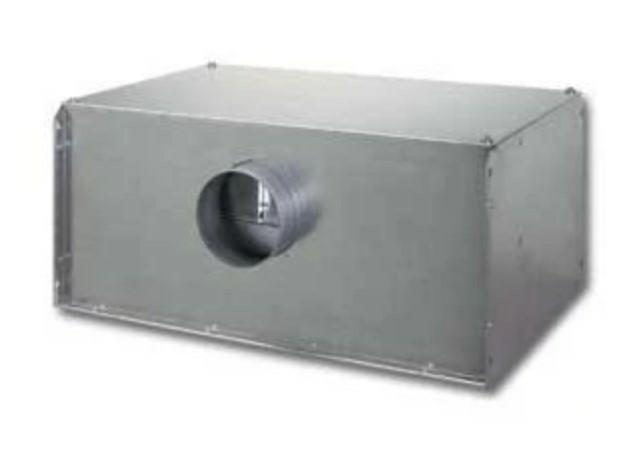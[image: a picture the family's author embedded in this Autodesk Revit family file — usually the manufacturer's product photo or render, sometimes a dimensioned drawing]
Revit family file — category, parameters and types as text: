
# Revit family: CADS_Vent-Axia_MechEquip_Fan_QPTW_QuietPackTwin - SUPPLY
name_source: partatom
category: Mechanical Equipment
units: mm (PartAtom-declared; Revit-internal decimal feet)

## family parameters
Classification = None
Cut with Voids When Loaded = No
Host = Face
OmniClass Number = 23.75.35.17.11
OmniClass Title = Fans for Air Ductwork
Part Type = Normal
Room Calculation Point = No
Round Connector Dimension = Use Diameter
Shared = No

## types (7) — shared parameters
Air Flow = 0.0 L/s
AirflowRateRange = 0.0 L/s
AssemblyPlace = UNKNOWN
AssetType = FIXED
Default Elevation = 1219 mm
DurationUnit = Year
EBHoffset = 206 mm
EBVoffset = 80 mm
ExteriorInsulation = No
Fitting Type = Ignore
GrossWeight = 0.00 kg
HasProtectiveEarth = No
IsExtendedWarranty = No
ManufacturerAddress = Fleming Way
Crawley 
RH10 9YX
Quantity = 1
RatedCurrent = 0 A
RatedVoltage = 0 V
Status = New
WarrantyGuarantor = Vent-Axia Limited
WorkingPressure = 0.0 Pa
zero-valued in all types: CADS_Index, CADS_Usage, ExpectedServiceLife, H, NumberOfPoles, OutOffset, W

## per-type parameters (varying)
| type | L | ModelReference | NominalDiameter | NominalHeight | NominalLength | NominalWidth | SpigotCLHeight | Type Image |
| QPTW100C | 590 mm  [stored 1.9357 ft] | QPTW100C QUIET PACK TWIN FAN | 100 mm  [stored 0.328084 ft] | 256 mm  [stored 0.839895 ft] | 610 mm  [stored 2.00131 ft] | 622 mm  [stored 2.04068 ft] | 128 mm  [stored 0.419948 ft] | <None> |
| QPTW125C | 590 mm  [stored 1.9357 ft] | QPTW125C QUIET PACK TWIN FAN | 125 mm  [stored 0.410105 ft] | 256 mm  [stored 0.839895 ft] | 610 mm  [stored 2.00131 ft] | 622 mm  [stored 2.04068 ft] | 128 mm  [stored 0.419948 ft] | <None> |
| QPTW150C | 590 mm  [stored 1.9357 ft] | QPTW150C QUIET PACK TWIN FAN | 150 mm | 256 mm  [stored 0.839895 ft] | 610 mm  [stored 2.00131 ft] | 622 mm  [stored 2.04068 ft] | 128 mm  [stored 0.419948 ft] | <None> |
| QPTW160C | 590 mm  [stored 1.9357 ft] | QPTW160C QUIET PACK TWIN FAN | 160 mm  [stored 0.524934 ft] | 256 mm  [stored 0.839895 ft] | 610 mm  [stored 2.00131 ft] | 622 mm  [stored 2.04068 ft] | 128 mm  [stored 0.419948 ft] | <None> |
| QPTW250C | 905 mm  [stored 2.96916 ft] | QPTW250C QUIET PACK TWIN FAN | 250 mm  [stored 0.82021 ft] | 354 mm  [stored 1.16142 ft] | 925 mm  [stored 3.03478 ft] | 829 mm  [stored 2.71982 ft] | 177 mm  [stored 0.580709 ft] | <None> |
| QPTW315C | 1235 mm  [stored 4.05184 ft] | QPTW315C QUIET PACK TWIN FAN | 315 mm  [stored 1.03346 ft] | 536 mm  [stored 1.75853 ft] | 1255 mm  [stored 4.11745 ft] | 1176 mm  [stored 3.85827 ft] | 268 mm | <None> |
| QPTW400C | 1235 mm  [stored 4.05184 ft] | QPTW400C QUIET PACK TWIN FAN | 400 mm  [stored 1.31234 ft] | 536 mm  [stored 1.75853 ft] | 1255 mm  [stored 4.11745 ft] | 1176 mm  [stored 3.85827 ft] | 268 mm | CADS_Vent-Axia_MechEquip_Fan_QPTW_QuietPackTwin.jpg |

note: column(s) folded — value = type name in every type: ModelNumber

note: [stored X ft] marks values corroborated as IEEE doubles in the binary element streams (Revit-internal decimal feet)

## geometry (parser evidence)
native form markers: Sweep x4
no freeform markers — native parametric forms only
